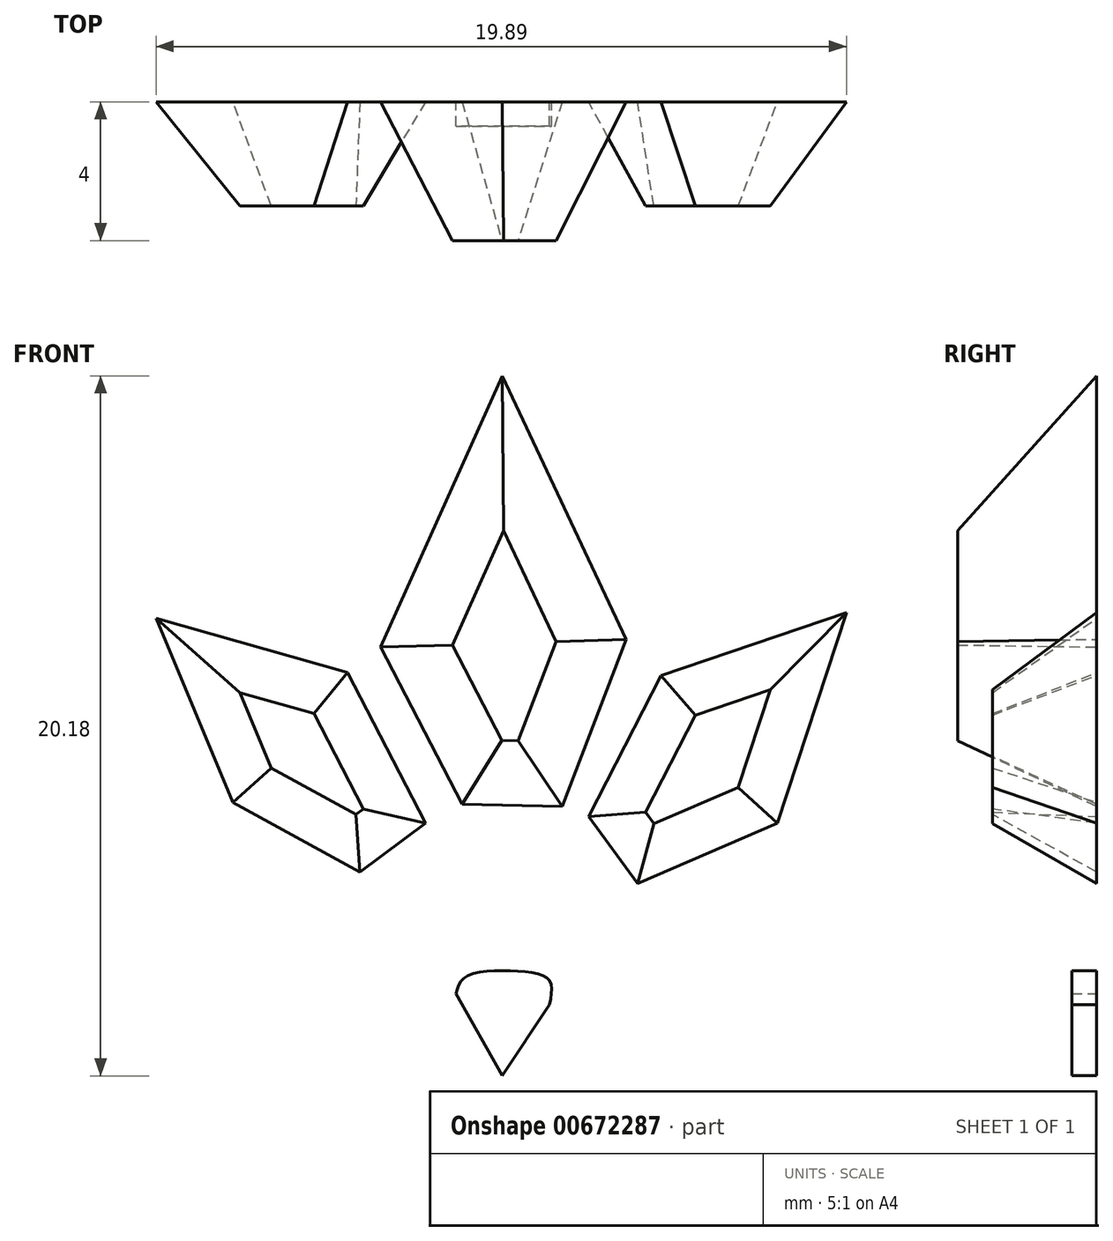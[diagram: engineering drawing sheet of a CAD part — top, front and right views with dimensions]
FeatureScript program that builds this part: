
annotation { "Feature Type Name" : "Feature", "Feature Type Description" : "" }
export const myFeature = defineFeature(function(context is Context, id is Id, definition is map)
    precondition{}
    {
        {
            var Q0;
            Q0=qCreatedBy(makeId("Front.planeOp"),FACE);
            var Q1;
            Q1 = qBodyType(qCreatedBy(id + "F1" ,EDGE), BodyType.WIRE);
            cPlane(context, id + "F0", {"entities" : qUnion([Q0, Q1]), "cplaneType" : CPlaneType.OFFSET, "offset" : 0.1 * mm, "width" : 150 * mm, "height" : 150 * mm});
        }
        {
            var Q0;
            Q0=qCreatedBy(id+"F0.planeOp",FACE);
            var sketch = newSketch(context, id + "F1", { "sketchPlane" : qUnion([Q0])});
            skLineSegment(sketch, "E0", {"start": v(-4.1, 13.4) * mm, "end": v(-7.76, 15.42) * mm});
            skLineSegment(sketch, "E1", {"start": v(-7.76, 15.42) * mm, "end": v(-9.97, 20.72) * mm});
            skLineSegment(sketch, "E2", {"start": v(-9.97, 20.72) * mm, "end": v(-4.46, 19.15) * mm});
            skLineSegment(sketch, "E3", {"start": v(-4.46, 19.15) * mm, "end": v(-2.21, 14.81) * mm});
            skLineSegment(sketch, "E4", {"start": v(-2.21, 14.81) * mm, "end": v(-1.16, 15.36) * mm});
            skLineSegment(sketch, "E5", {"start": v(-1.16, 15.36) * mm, "end": v(-3.5, 19.9) * mm});
            skLineSegment(sketch, "E6", {"start": v(-3.5, 19.9) * mm, "end": v(0, 27.71) * mm});
            skLineSegment(sketch, "E7", {"start": v(0, 27.71) * mm, "end": v(3.58, 20.12) * mm});
            skLineSegment(sketch, "E8", {"start": v(3.58, 20.12) * mm, "end": v(1.73, 15.3) * mm});
            skLineSegment(sketch, "E9", {"start": v(1.73, 15.3) * mm, "end": v(2.49, 15) * mm});
            skLineSegment(sketch, "E10", {"start": v(2.49, 15) * mm, "end": v(4.58, 19.07) * mm});
            skLineSegment(sketch, "E11", {"start": v(4.58, 19.07) * mm, "end": v(9.92, 20.88) * mm});
            skLineSegment(sketch, "E12", {"start": v(9.92, 20.88) * mm, "end": v(7.93, 14.81) * mm});
            skLineSegment(sketch, "E13", {"start": v(7.93, 14.81) * mm, "end": v(3.9, 13.08) * mm});
            skFitSpline(sketch, "E14", {"points": [v(-4.1, 13.4) * mm, v(-3.68, 11.24) * mm, v(-3.57, 8.1) * mm, v(-3.45, 7.09) * mm], "startDerivative": vector(1.45, -5.65) * mm, "endDerivative": vector(0.57, -3.59) * mm});
            skFitSpline(sketch, "E15", {"points": [v(3.9, 13.08) * mm, v(3.58, 10.95) * mm, v(3.58, 7.94) * mm], "startDerivative": vector(-0.86, -4.43) * mm, "endDerivative": vector(0.2, -5.8) * mm});
            skLineSegment(sketch, "E16", {"start": v(-4.1, 13.4) * mm, "end": v(-2.21, 14.81) * mm});
            skLineSegment(sketch, "E17", {"start": v(-1.16, 15.36) * mm, "end": v(1.73, 15.3) * mm});
            skLineSegment(sketch, "E18", {"start": v(3.9, 13.08) * mm, "end": v(2.49, 15) * mm});
            skLineSegment(sketch, "E19", {"start": v(-1.34, 9.9) * mm, "end": v(0, 7.53) * mm});
            skLineSegment(sketch, "E20", {"start": v(0, 7.53) * mm, "end": v(1.36, 9.59) * mm});
            skFitSpline(sketch, "E21", {"points": [v(1.36, 9.59) * mm, v(1.36, 10.28) * mm, v(0.48, 10.54) * mm, v(-1.03, 10.4) * mm, v(-1.34, 9.9) * mm], "startDerivative": vector(0.74, 3.63) * mm, "endDerivative": vector(-0.86, -2.85) * mm});
            skSolve(sketch);
        }
        {
            var Q0;
            Q0=makeQuery(id+"F1.imprint","IMPRINT",FACE,{"disambiguationData":[TD([[makeQuery(id+"F1.imprint","IMPRINT",EDGE,{"derivedFrom":sQuery(id+"F1.wireOp",EDGE,"E0")}),-1.0]])]});
            extrude(context, id + "F2", {"entities" : qUnion([Q0]), "depth" : 3 * mm, "offsetDistance" : 25 * mm, "hasDraft" : true, "draftAngle" : 25 * degree, "draftPullDirection" : true});
        }
        {
            var Q0;
            Q0=makeQuery(id+"F1.imprint","IMPRINT",FACE,{"disambiguationData":[TD([[makeQuery(id+"F1.imprint","IMPRINT",EDGE,{"derivedFrom":sQuery(id+"F1.wireOp",EDGE,"E5")}),-1.0]])]});
            extrude(context, id + "F3", {"entities" : qUnion([Q0]), "depth" : 4 * mm, "offsetDistance" : 25 * mm, "hasDraft" : true, "draftAngle" : 25 * degree, "draftPullDirection" : true});
        }
        {
            var Q0;
            Q0=makeQuery(id+"F1.imprint","IMPRINT",FACE,{"disambiguationData":[TD([[makeQuery(id+"F1.imprint","IMPRINT",EDGE,{"derivedFrom":sQuery(id+"F1.wireOp",EDGE,"E10")}),-1.0]])]});
            extrude(context, id + "F4", {"entities" : qUnion([Q0]), "depth" : 3 * mm, "offsetDistance" : 25 * mm, "hasDraft" : true, "draftAngle" : 25 * degree, "draftPullDirection" : true});
        }
        {
            var Q0;
            Q0=makeQuery(id+"F1.imprint","IMPRINT",FACE,{"disambiguationData":[TD([[makeQuery(id+"F1.imprint","IMPRINT",EDGE,{"derivedFrom":sQuery(id+"F1.wireOp",EDGE,"E19")}),1.0]])]});
            extrude(context, id + "F5", {"entities" : qUnion([Q0]), "depth" : 0.71 * mm, "offsetDistance" : 25 * mm});
        }
    });
